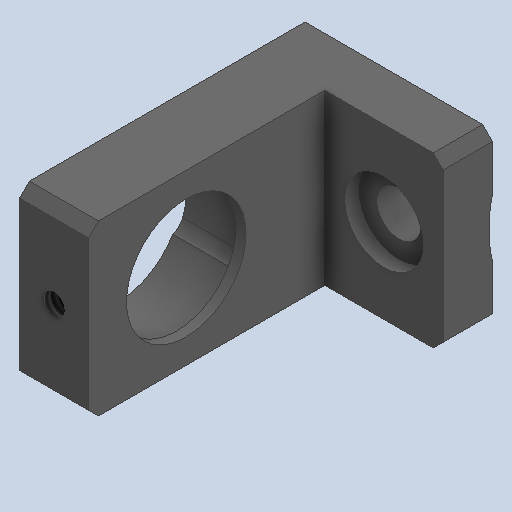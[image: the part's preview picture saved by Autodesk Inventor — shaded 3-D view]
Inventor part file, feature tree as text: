
AUTODESK INVENTOR PART (.ipt)
format: ipt  version: 2024.2 (Build 282272000, 272)  size: 355,328 bytes
history: native  units: in
note: dims shown in document units (in); Inventor stores cm internally (conversion verified against a paired STEP export)
features: extrude x6, hole x3, other x2, chamfer x1
ambient origin geometry x8: Origin, YZ Plane, XZ Plane, XY Plane, X Axis, Y Axis, Z Axis, Center Point
bodies: Solid1 (feature_tree)
feature tree (12):
  other  "Table"
  other  "ADAPTER_fixed-mirror-BH19.05-D12.7"
  extrude  "Extrusion1"  TaperAngle=0.0deg  [1 undecoded]
  extrude  "Extrusion2"  Depth=0.3371in
  extrude  "Extrusion3"  TaperAngle=0.0deg  [1 undecoded]
  extrude  "Extrusion4"  Depth=0.6742in
  hole  "Hole1"  [1 undecoded]
  hole  "Hole2"  [1 undecoded]
  hole  "Hole4"  [1 undecoded]
  extrude  "Extrusion5"  Depth=0.1201in
  chamfer  "Chamfer1"  Distance=0.75in
  extrude  "Extrusion6"  Depth=0.1374in
note: 5 required parameter values undecoded (feature->parameter linkage not recoverable at this tier; creation-order binding heuristic only, values carry confidence <= 0.55)
